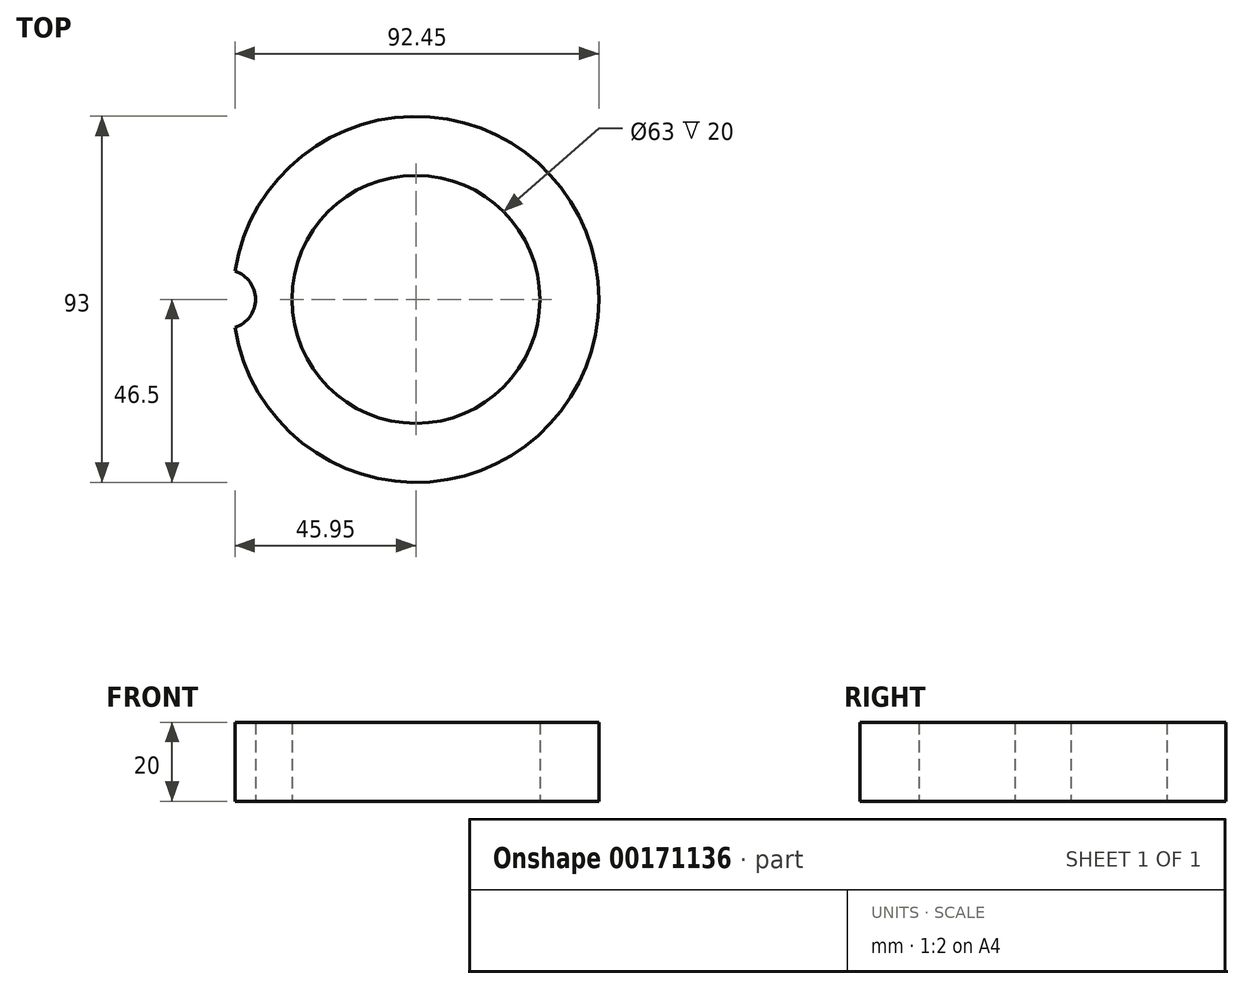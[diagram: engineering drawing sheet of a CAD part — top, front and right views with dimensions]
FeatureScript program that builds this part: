
annotation { "Feature Type Name" : "Feature", "Feature Type Description" : "" }
export const myFeature = defineFeature(function(context is Context, id is Id, definition is map)
    precondition{}
    {
        {
            var Q0;
            Q0=qCreatedBy(makeId("Top.planeOp"),FACE);
            var sketch = newSketch(context, id + "F0", { "sketchPlane" : qUnion([Q0])});
            skCircle(sketch, "E0", {"center": v(0, 0) * mm, "radius": 31.5 * mm});
            skCircle(sketch, "E1", {"center": v(0, 0) * mm, "radius": 46.5 * mm});
            skCircle(sketch, "E2", {"center": v(-48.25, 0) * mm, "radius": 7.5 * mm});
            skCircle(sketch, "E3", {"center": v(-48.25, 0) * mm, "radius": 11.5 * mm});
            skSolve(sketch);
        }
        {
            var Q0;
            {var subQ0=sQuery(id+"F0.wireOp",EDGE,"E2");var subQ1=sQuery(id+"F0.wireOp",EDGE,"E1");var subQ2=makeQuery(id+"F0.imprint","INTERSECT",VERTEX,{"disambiguationData":[OD(0.0)],"derivedFrom":[subQ1,subQ0]});Q0=makeQuery(id+"F0.imprint","IMPRINT",FACE,{"disambiguationData":[TD([[makeQuery(id+"F0.imprint","IMPRINT",EDGE,{"disambiguationData":[TD([[subQ2,1.0]])],"derivedFrom":subQ1}),1.0]])]});}
            var Q1;
            Q1=makeQuery(id+"F0.imprint","IMPRINT",FACE,{"disambiguationData":[TD([[makeQuery(id+"F0.imprint","IMPRINT",EDGE,{"derivedFrom":sQuery(id+"F0.wireOp",EDGE,"E0")}),-1.0]])]});
            extrude(context, id + "F1", {"entities" : qUnion([Q0, Q1]), "depth" : 20 * mm});
        }
    });
